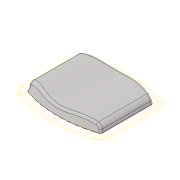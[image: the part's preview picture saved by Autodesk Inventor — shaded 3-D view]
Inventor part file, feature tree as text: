
AUTODESK INVENTOR PART (.ipt)
format: ipt  version: 2017 (Build 210142000, 142)  size: 1,267,200 bytes
history: native  units: in
note: dims shown in document units (in); Inventor stores cm internally (conversion verified against a paired STEP export)
features: other x6, sketch x4, fillet x3, extrude x2, surface_op x1, mirror x1, shell x1
ambient origin geometry x8: Origin, YZ Plane, XZ Plane, XY Plane, X Axis, Y Axis, Z Axis, Center Point
bodies: Solid1 (feature_tree)
feature tree (18):
  extrude  "Extrusion1"  Depth=20.0in
  surface_op  "Replace Face1"
  fillet  "Fillet1"  Radius=30.0in
  fillet  "Fillet2"  Radius=3.15in
  fillet  "Fillet3"  Radius=2.5in
  mirror  "Mirror1"
  shell  "Shell1"  Thickness=2.0in
  other  "Boss1"
  other  "Lip1"
  other  "Grill1"
  other  "Ruled Surface1"
  sketch  "Sketch1"  dims[d0=14.0in d1=20.0in d2=30.0in d3=3.15in d4=-0.0687in d5=2.5in d6=2.0in]
  sketch  "Sketch2"  dims[d7=6.5in d8=10.5in]
  other  "Srf1"
  sketch  "Sketch3"  dims[d9=10.0in]
  sketch  "Sketch4"  dims[d10=2.15in d11=2.15in d12=1.5in d13=3.0in d14=1.375in d15=17.0in d16=0.0in d17=1.5in d18=1.5in d19=0.6in d20=0.6in d21=1.0in d22=0.3937in d23=0.8in d24=0.3283in d25=0.2in d26=16.0in d27=11.0in d28=0.0in d29=0.0in d30=0.4in d31=0.2in d32=0.38in d33=0.0137in d34=0.0069in d35=1.1811in d37=0.12in d38=0.8in d39=0.4in d40=0.0in d41=0.0344in d42=0.0172in d43=0.04in d44=0.04in d45=0.0in d46=360.0deg d47=0.12in d48=0.1in d49=0.0in d50=0.0137in d51=0.0687in d52=0.0in d53=1.2in d54=8.0in d55=0.4in d56=0.4in d57=0.3in d58=6.5787in d59=0.15in d60=0.4in d61=0.0in d62=0.08in d63=0.2in d64=0.0in d65=0.15in d66=0.0in d67=0.0in d68=0.05in d69=0.0in d70=0.0in d71=0.0in d72=18.288in d73=2.0in d74=0.0in]
  other  "Srf2"
  extrude  "ExtrusionSrf1"  Depth=10.5in
